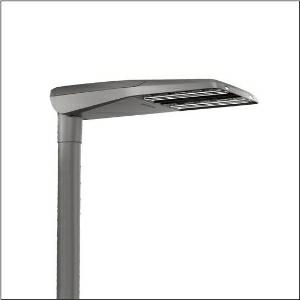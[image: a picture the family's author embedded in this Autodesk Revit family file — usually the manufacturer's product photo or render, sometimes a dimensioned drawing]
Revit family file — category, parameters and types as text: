
# Revit family: streetlight_sl_11_iq_midi___st1_2a_5xc3a41e08me_8609
name_source: partatom
category: Lighting Fixtures
units: mm (PartAtom-declared; Revit-internal decimal feet)

## family parameters
Cut with Voids When Loaded = No
Host = Face
Light Source = No
Part Type = Normal
Room Calculation Point = No
Round Connector Dimension = Use Diameter
Shared = No

## types (1)
- --- (1 x LED, 18900 lm, 124.7 W, 4000K)
    Apparent Load = 125 VA
    CIE Flux Codes = 32 70 96 100 100
    Color Rendering = 70
    Color Temperature = 4000K
    Default Elevation = 1800 mm
    Description = Streetlight SL 11 iQ midi, mast luminaire, primary light control with 3 zone facetted reflector, of plastic, silver coated, highly specular, primary optical cover: cover, of PMMA, transparent, light distribution: ST1.2a, light emission: direct distribution, primary light characteristic: asymmetric, installation type: post-top, side-entry, LED, High Power LED, rated luminous flux: 18.900lm, luminous efficacy: 152lm/W, light colour: 740, colour temperature: 4000K, control: optimised constant luminous flux control (CLO 2.0), Desk-Remote (wireless, voltage-free reading and setting of iQ features in the workshop via application-optimized NFC function/RFID function), Light-Fading, Smart-Wire, Night-Set, Lumen-Switch, Temp-Guard, Auto-Match, with cable H07RN-F 5x 1.5mm², mains connection: 220..240V, AC, 50/60Hz, connection cable pre-assembled, cable length: 12,5m, start of lifetime: 125W, end of lifetime: 132W, reduction: 57W, luminaire housing, of diecast aluminium, powder-coated, Siteco® metallic grey (DB 702S), length: 780mm, width: 376mm, height: 118mm, spigot size: 60/76mm (post-top) and 42/60/76mm (side-entry), mast flange for spigot size: 42mm: 5XC10008XM4, 60mm: 5XC10008XM2, 76/60mm: 5XC10108XM1, equipment: Power, protection rating (complete): IP66, insulation class (complete): insulation class II (safety insulation), certification: CE, ENEC, VDE, impact resistance: IK09, permissible operating ambient temperature for outdoor applications: -25..+50°C, standard-compliant lighting for roads and squares, packaging unit: 1 piece

Light Distribution: ST1.2a
    Height = 118 mm
    Lamp = 1 x LED
    Lamp Light Flux = 18900 lm
    Lamp Power = 124.7 W
    Lamp count = 1
    Length = 780 mm
    Luminous efficacy = 152 lm/W
    Manufacturer = Siteco
    ModVariant = No
    Model = 5XC3A41E08ME
    Number of Poles = 1
    OnlyDefault = Yes
    Power Factor = 1
    Product Name = Streetlight SL 11 iQ midi | ST1.2a
    Product group = mast luminaire | pylon top
    ProductGroupID = 6100
    Protection Class = Protection class II
    Protection Degree = IP 66
    RLX_Detail_Level = 1
    RlxData = <blob elided: 70441 chars, md5=a7e5d125>
    Socket = socket
    Standby Power = 0 W
    System Light Flux = 18900 lm
    System Power = 125 W
    Type Comments = factory setting: luminous flux: 100 % | dim-lin: 254 | 557 mA
    Type Image = l_1005960.jpg
    URL = http://relux.com
    VarID = @adj_119039
    Voltage = 0 V
    Weight = 0.00 kg
    Width = 376 mm

## geometry (parser evidence)
native form markers: Blend x4, Sweep x10
no freeform markers — native parametric forms only
